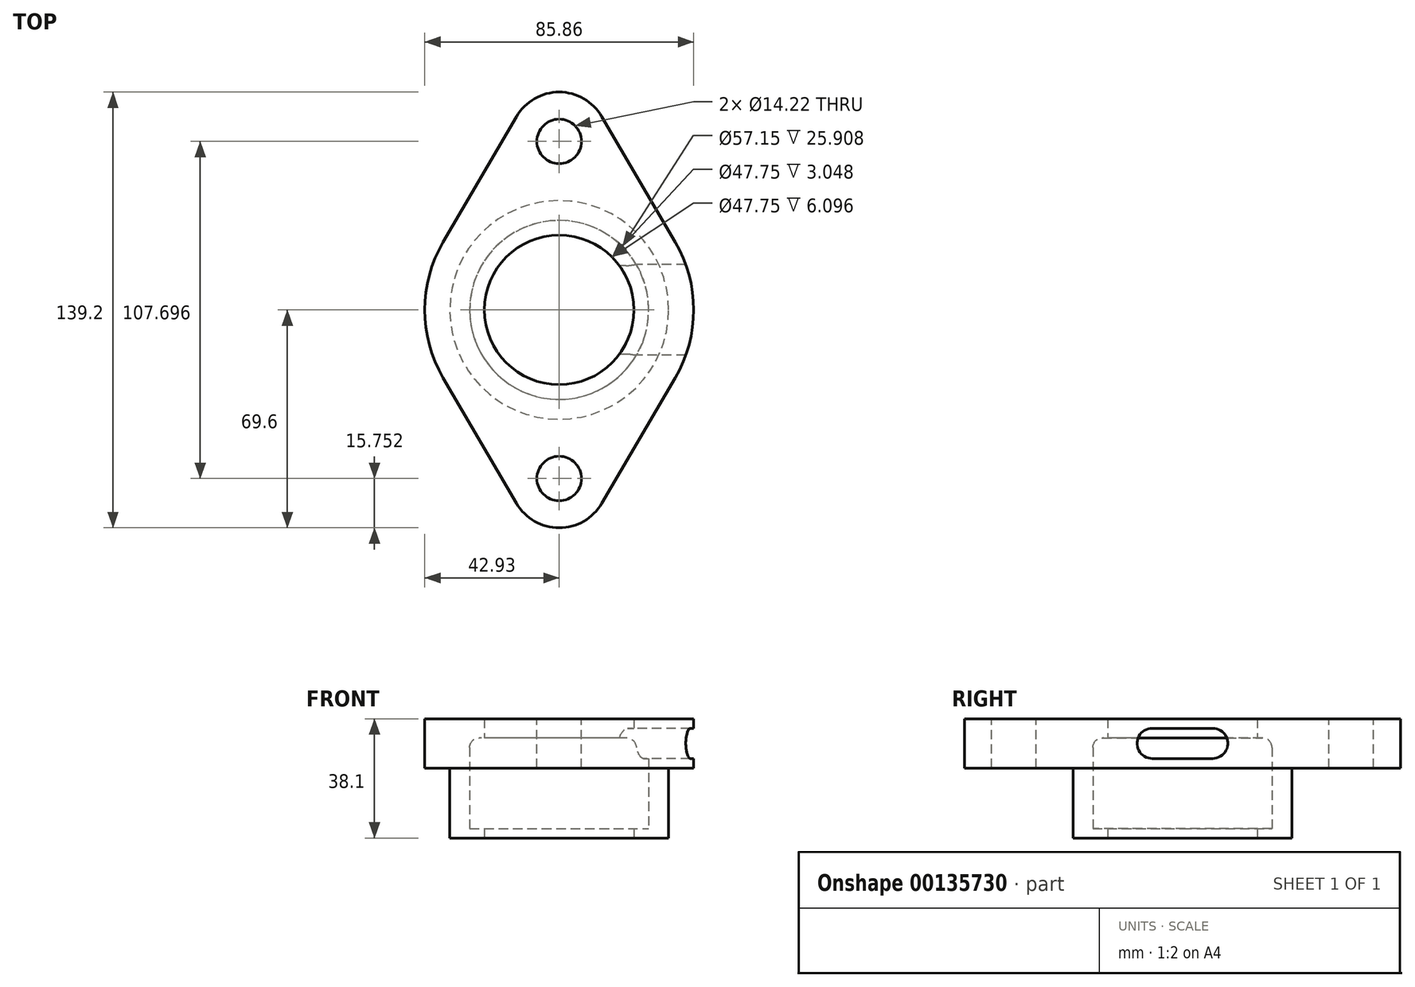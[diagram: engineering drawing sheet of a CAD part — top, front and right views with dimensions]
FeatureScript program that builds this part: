
annotation { "Feature Type Name" : "Feature", "Feature Type Description" : "" }
export const myFeature = defineFeature(function(context is Context, id is Id, definition is map)
    precondition{}
    {
        {
            var Q0;
            Q0=qCreatedBy(makeId("Front.planeOp"),FACE);
            var sketch = newSketch(context, id + "F0", { "sketchPlane" : qUnion([Q0])});
            skLineSegment(sketch, "E0", {"start": v(0, 0) * mm, "end": v(0, 77.1) * mm, "construction": true});
            skLineSegment(sketch, "E1", {"start": v(0, 0) * mm, "end": v(-34.93, 0) * mm});
            skLineSegment(sketch, "E2", {"start": v(-34.93, 0) * mm, "end": v(-34.93, 22.35) * mm});
            skLineSegment(sketch, "E3", {"start": v(-34.93, 22.35) * mm, "end": v(-42.93, 22.35) * mm});
            skLineSegment(sketch, "E4", {"start": v(-42.93, 22.35) * mm, "end": v(-42.93, 38.1) * mm});
            skLineSegment(sketch, "E5", {"start": v(-42.93, 38.1) * mm, "end": v(-23.88, 38.1) * mm});
            skLineSegment(sketch, "E6", {"start": v(-23.88, 38.1) * mm, "end": v(-23.88, 35.05) * mm});
            skLineSegment(sketch, "E7", {"start": v(-23.88, 35.05) * mm, "end": v(0, 35.05) * mm});
            skLineSegment(sketch, "E8", {"start": v(0, 35.05) * mm, "end": v(0, 0) * mm});
            skLineSegment(sketch, "E9", {"start": v(0, 3.05) * mm, "end": v(-28.57, 3.05) * mm});
            skLineSegment(sketch, "E10", {"start": v(-28.57, 3.05) * mm, "end": v(-28.57, 32) * mm});
            skLineSegment(sketch, "E11", {"start": v(-28.57, 32) * mm, "end": v(0, 32) * mm});
            skLineSegment(sketch, "E12", {"start": v(0, 32) * mm, "end": v(0, 3.05) * mm});
            skSolve(sketch);
        }
        {
            var Q0;
            {var subQ4=sQuery(id+"F0.wireOp",EDGE,"E1");Q0=makeQuery(id+"F0.imprint","IMPRINT",FACE,{"disambiguationData":[TD([[makeQuery(id+"F0.imprint","IMPRINT",EDGE,{"derivedFrom":subQ4}),-1.0]])]});}
            var Q1;
            Q1=sQuery(id+"F0.wireOp",EDGE,"E0");
            revolve(context, id + "F1", {"entities" : qUnion([Q0]), "axis" : qUnion([Q1]), "revolveType" : RevolveType.FULL});
        }
        {
            var Q0;
            Q0=makeQuery(id+"F1.opRevolve","SWEPT_FACE",FACE,{"disambiguationData":[OSD([sQuery(id+"F0.wireOp",EDGE,"E5")])]});
            var sketch = newSketch(context, id + "F2", { "sketchPlane" : qUnion([Q0])});
            skLineSegment(sketch, "E13", {"start": v(0, 0) * mm, "end": v(0, 53.85) * mm, "construction": true});
            skLineSegment(sketch, "E14", {"start": v(0, 0) * mm, "end": v(0, -53.85) * mm, "construction": true});
            skCircle(sketch, "E15", {"center": v(0, 53.85) * mm, "radius": 7.11 * mm});
            skCircle(sketch, "E16", {"center": v(0, -53.85) * mm, "radius": 7.11 * mm});
            skLineSegment(sketch, "E17", {"start": v(-37.06, 21.67) * mm, "end": v(-13.6, 61.8) * mm});
            skLineSegment(sketch, "E18", {"start": v(37.06, 21.67) * mm, "end": v(13.6, 61.8) * mm});
            skLineSegment(sketch, "E19", {"start": v(37.06, -21.67) * mm, "end": v(13.6, -61.8) * mm});
            skLineSegment(sketch, "E20", {"start": v(-37.06, -21.67) * mm, "end": v(-13.6, -61.8) * mm});
            skArc(sketch, "E21", {"start": v(13.6, 61.8) * mm, "mid": v(0, 69.6) * mm, "end": v(-13.6, 61.8) * mm});
            skArc(sketch, "E22", {"start": v(-13.6, -61.8) * mm, "mid": v(0, -69.6) * mm, "end": v(13.6, -61.8) * mm});
            skSolve(sketch);
        }
        {
            var Q0;
            Q0=makeQuery(id+"F2.imprint","IMPRINT",FACE,{"disambiguationData":[TD([[makeQuery(id+"F2.imprint","IMPRINT",EDGE,{"derivedFrom":sQuery(id+"F2.wireOp",EDGE,"E15")}),-1.0]])]});
            var Q1;
            Q1=makeQuery(id+"F2.imprint","IMPRINT",FACE,{"disambiguationData":[TD([[makeQuery(id+"F2.imprint","IMPRINT",EDGE,{"derivedFrom":sQuery(id+"F2.wireOp",EDGE,"E16")}),-1.0]])]});
            extrude(context, id + "F3", {"entities" : qUnion([Q0, Q1]), "operationType" : NewBodyOperationType.ADD, "oppositeDirection" : true, "depth" : 15.75 * mm});
        }
        {
            var Q0;
            Q0=makeQuery(id+"F1.opRevolve","SWEPT_FACE",FACE,{"disambiguationData":[OSD([sQuery(id+"F0.wireOp",EDGE,"E1")])]});
            var sketch = newSketch(context, id + "F4", { "sketchPlane" : qUnion([Q0])});
            skCircle(sketch, "E23", {"center": v(0, 0) * mm, "radius": 23.88 * mm});
            skSolve(sketch);
        }
        {
            var Q0;
            Q0=makeQuery(id+"F4.imprint","IMPRINT",FACE,{"disambiguationData":[TD([[makeQuery(id+"F4.imprint","IMPRINT",EDGE,{"derivedFrom":sQuery(id+"F4.wireOp",EDGE,"E23")}),1.0]])]});
            extrude(context, id + "F5", {"entities" : qUnion([Q0]), "operationType" : NewBodyOperationType.REMOVE, "oppositeDirection" : true, "depth" : 3.05 * mm});
        }
        {
            var Q0;
            Q0=makeQuery(id+"F5.boolean.opBoolean","COPY",EDGE,{"derivedFrom":makeQuery(id+"F5.opExtrude","CAP_EDGE",EDGE,{"disambiguationData":[OSD([sQuery(id+"F4.wireOp",EDGE,"E23")])],"isStart":false})});
            var Q1;
            Q1=makeQuery(id+"F1.opRevolve","SWEPT_EDGE",EDGE,{"disambiguationData":[OSD([sQuery(id+"F0.wireOp",EDGE,"E10"),sQuery(id+"F0.wireOp",EDGE,"E11")])]});
            fillet(context, id + "F6", {"entities" : qUnion([Q0, Q1]), "radius" : 3.05 * mm, "tangentPropagation" : true, "allowEdgeOverflow" : false});
        }
        {
            var Q0;
            Q0=qCreatedBy(makeId("Right.planeOp"),FACE);
            var sketch = newSketch(context, id + "F7", { "sketchPlane" : qUnion([Q0])});
            skLineSegment(sketch, "E24", {"start": v(0, 0) * mm, "end": v(0, 30.23) * mm, "construction": true});
            skLineSegment(sketch, "E25", {"start": v(0, 30.23) * mm, "end": v(0, 38.1) * mm, "construction": true});
            skLineSegment(sketch, "E26", {"start": v(0, 30.23) * mm, "end": v(-9.65, 30.23) * mm, "construction": true});
            skLineSegment(sketch, "E27", {"start": v(0, 30.23) * mm, "end": v(9.65, 30.23) * mm, "construction": true});
            skCircle(sketch, "E28", {"center": v(-9.65, 30.23) * mm, "radius": 4.83 * mm});
            skCircle(sketch, "E29", {"center": v(9.65, 30.23) * mm, "radius": 4.83 * mm});
            skLineSegment(sketch, "E30", {"start": v(-9.65, 35.05) * mm, "end": v(9.65, 35.05) * mm});
            skLineSegment(sketch, "E31", {"start": v(-9.65, 25.4) * mm, "end": v(9.65, 25.4) * mm});
            skSolve(sketch);
        }
        {
            var Q0;
            Q0 = qSketchRegion(id + "F7", true);
            extrude(context, id + "F8", {"entities" : qUnion([Q0]), "operationType" : NewBodyOperationType.REMOVE, "endBound" : BoundingType.THROUGH_ALL, "depth" : 25.4 * mm});
        }
        {
            var Q0;
            Q0=makeQuery(id+"F1.opRevolve","SWEPT_FACE",FACE,{"disambiguationData":[OSD([sQuery(id+"F0.wireOp",EDGE,"E7")])]});
            extrude(context, id + "F9", {"entities" : qUnion([Q0]), "operationType" : NewBodyOperationType.REMOVE, "oppositeDirection" : true, "depth" : 25.4 * mm});
        }
    });
